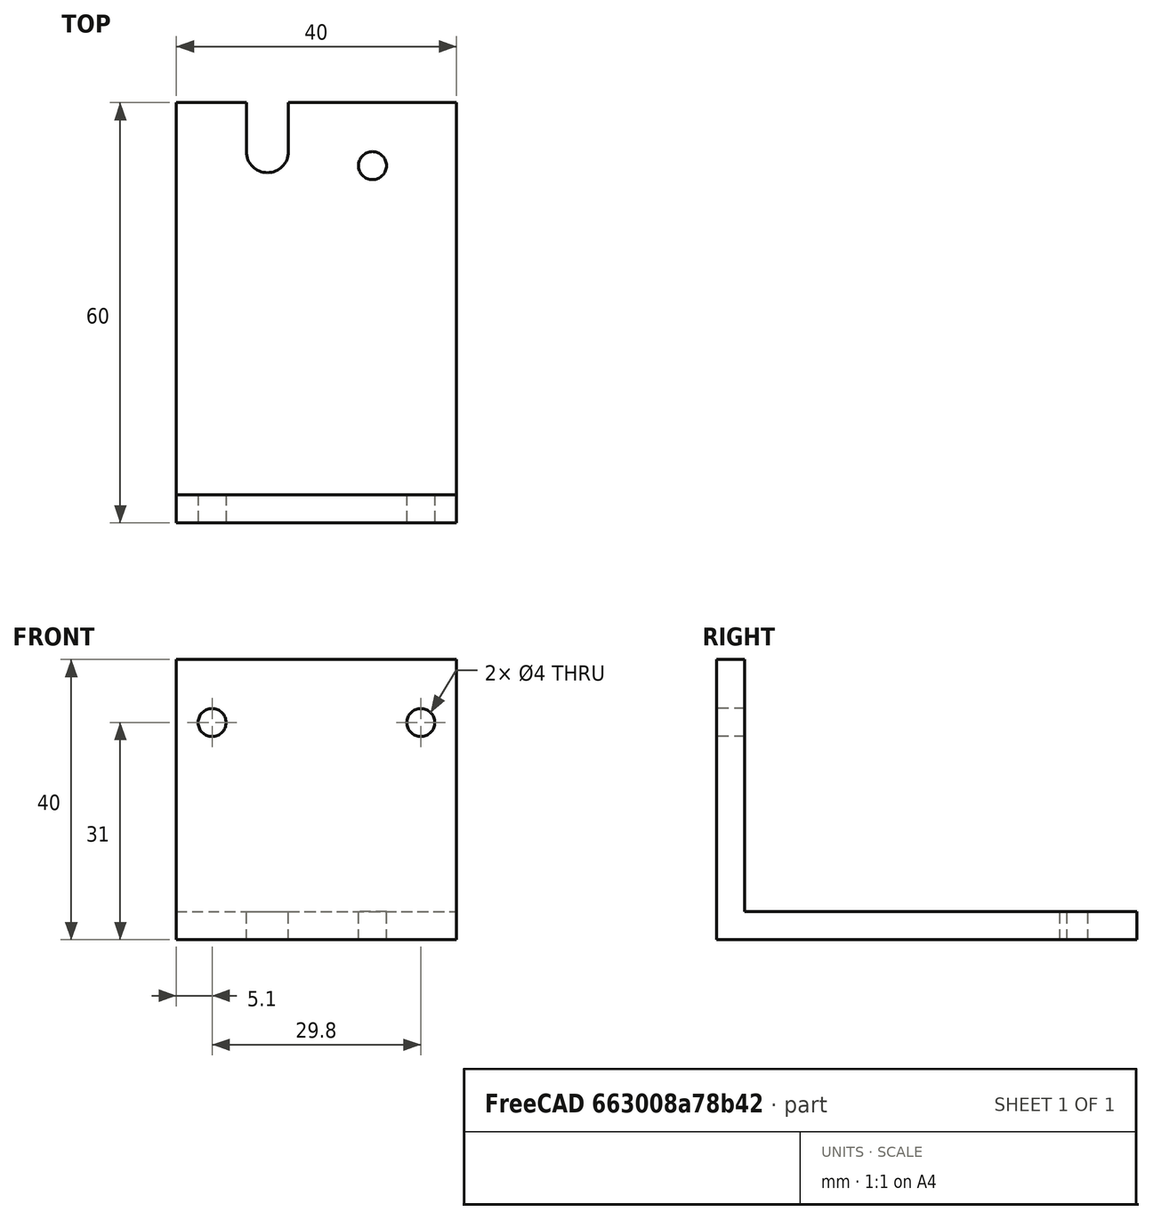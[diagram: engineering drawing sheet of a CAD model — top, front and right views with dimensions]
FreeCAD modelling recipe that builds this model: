
FCSTD DOCUMENT  (FreeCAD 0.15R4671 (Git))
Label: Soporte Extrusor
License: All rights reserved
LicenseURL: http://en.wikipedia.org/wiki/All_rights_reserved
objects: Part::Cylinder×4, Part::Box×3, Part::MultiFuse×3, Part::Cut×3
note: 13 computed .brp shape members not serialized (recipe doc carries the construction recipe); baked Part::Feature solids carry a one-line shape summary decoded from their .brp

FEATURE [Part::Box] Box  label="Cubo"
  Height = 4
  Length = 40
  Width = 60
FEATURE [Part::Box] Box001  label="Cubo001"
  Height = 40
  Length = 40
  Width = 4
FEATURE [Part::MultiFuse] Fusion
  Shapes = -> [Box001,Box]
FEATURE [Part::Cylinder] Cylinder  label="Agujero 2"
  Angle = 360
  Height = 4
  Placement = pos=(5.1,4,31) rot=(0.57735,-0.57735,0.57735;2.0944rad)
  Radius = 2
FEATURE [Part::Cylinder] Cylinder001  label="Agujero 1"
  Angle = 360
  Height = 4
  Placement = pos=(34.9,4,31) rot=(0.57735,-0.57735,0.57735;2.0944rad)
  Radius = 2
FEATURE [Part::MultiFuse] Fusion001  label="Agujeros roscados M4"
  Shapes = -> [Cylinder001,Cylinder]
FEATURE [Part::Cut] Cut
  Base = -> Fusion
  Tool = -> Fusion001
FEATURE [Part::Cylinder] Cylinder002  label="agujero de sujeccion"
  Angle = 360
  Height = 4
  Placement = pos=(28,51,0) rot=(0,0,1;0rad)
  Radius = 2
FEATURE [Part::Cylinder] Cylinder003  label="Cilindro003"
  Angle = 360
  Height = 4
  Placement = pos=(13,53,0) rot=(0,0,1;0rad)
  Radius = 3
FEATURE [Part::Box] Box002  label="Cubo002"
  Height = 4
  Length = 6
  Placement = pos=(10,53,0) rot=(0,0,1;0rad)
  Width = 7
FEATURE [Part::MultiFuse] Fusion002  label="Agujero de sujeccion del hotend"
  Shapes = -> [Box002,Cylinder003]
FEATURE [Part::Cut] Cut001
  Base = -> Cut
  Tool = -> Fusion002
FEATURE [Part::Cut] Cut002  label="Soporte Extrusor"
  Base = -> Cut001
  Tool = -> Cylinder002
